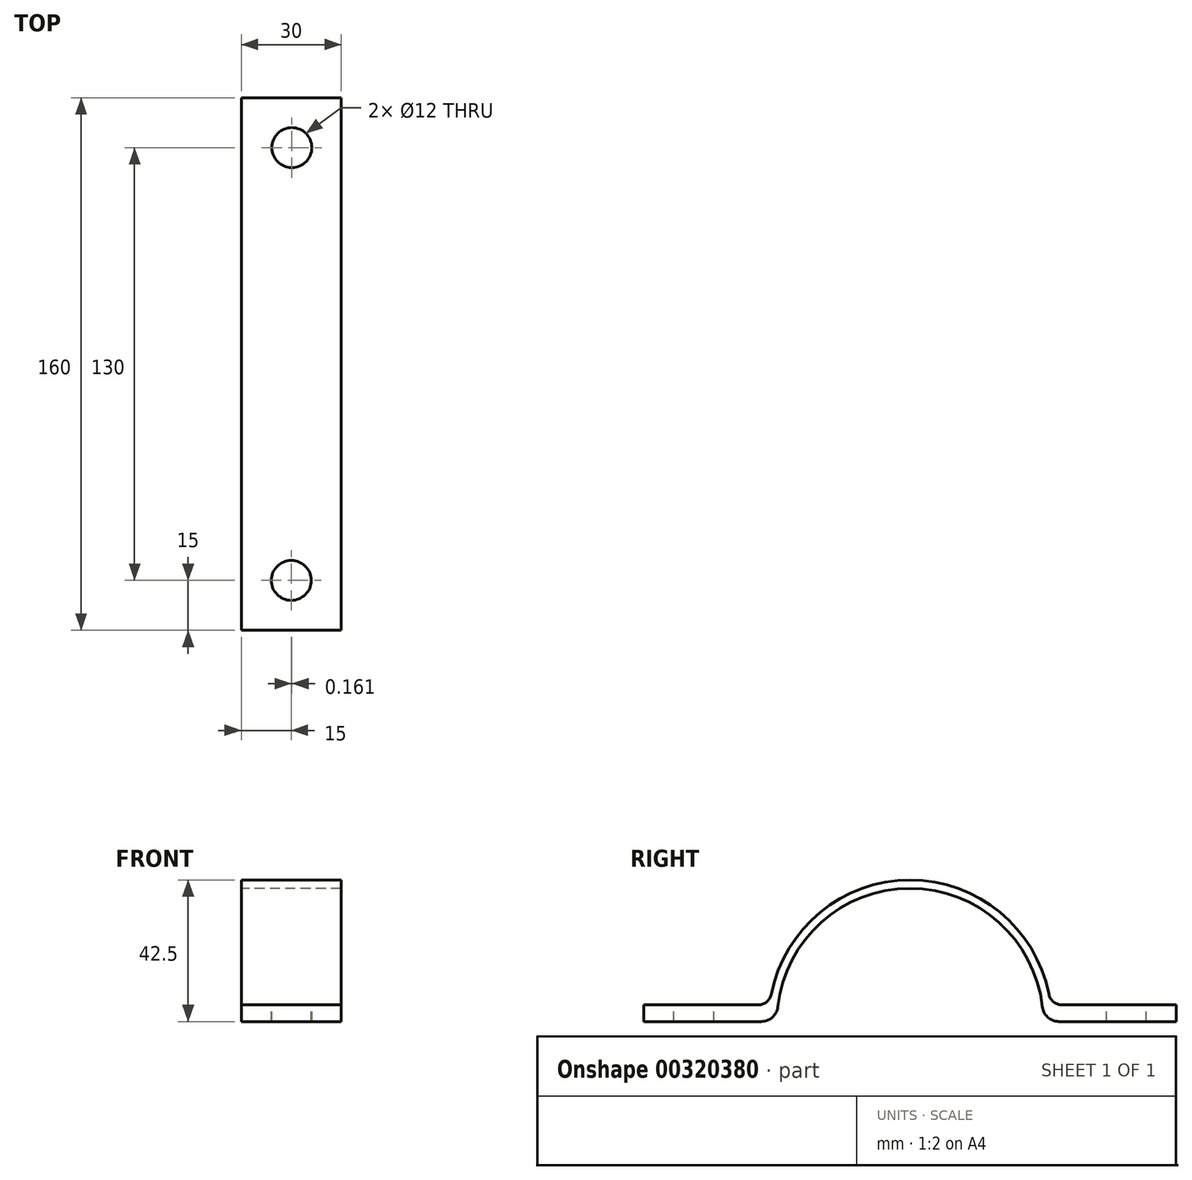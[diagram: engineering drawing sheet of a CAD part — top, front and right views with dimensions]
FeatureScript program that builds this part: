
annotation { "Feature Type Name" : "Feature", "Feature Type Description" : "" }
export const myFeature = defineFeature(function(context is Context, id is Id, definition is map)
    precondition{}
    {
        {
            var Q0;
            Q0=qCreatedBy(makeId("Right.planeOp"),FACE);
            var sketch = newSketch(context, id + "F0", { "sketchPlane" : qUnion([Q0])});
            skArc(sketch, "E0", {"start": v(42.2, 5) * mm, "mid": v(0, 42.5) * mm, "end": v(-42.2, 5) * mm});
            skArc(sketch, "E1", {"start": v(40, 0) * mm, "mid": v(0, 40) * mm, "end": v(-40, 0) * mm});
            skLineSegment(sketch, "E2.bottom", {"start": v(-80, 0) * mm, "end": v(-40, 0) * mm});
            skLineSegment(sketch, "E3.trimOffspring", {"start": v(40, 0) * mm, "end": v(80, 0) * mm});
            skLineSegment(sketch, "E4.top", {"start": v(-80, 5) * mm, "end": v(-42.2, 5) * mm});
            skLineSegment(sketch, "E4.left", {"start": v(-80, 0) * mm, "end": v(-80, 5) * mm});
            skLineSegment(sketch, "E4.right", {"start": v(80, 0) * mm, "end": v(80, 5) * mm});
            skLineSegment(sketch, "E5.trimOffspring", {"start": v(42.2, 5) * mm, "end": v(80, 5) * mm});
            skSolve(sketch);
        }
        {
            var Q0;
            Q0=makeQuery(id+"F0.imprint","IMPRINT",FACE,{"disambiguationData":[TD([[makeQuery(id+"F0.imprint","IMPRINT",EDGE,{"derivedFrom":sQuery(id+"F0.wireOp",EDGE,"E0")}),1.0]])]});
            extrude(context, id + "F1", {"entities" : qUnion([Q0]), "depth" : 30 * mm});
        }
        {
            var Q0;
            Q0=makeQuery(id+"F1.opExtrude","SWEPT_EDGE",EDGE,{"disambiguationData":[OSD([sQuery(id+"F0.wireOp",EDGE,"E0"),sQuery(id+"F0.wireOp",EDGE,"E4.top")])]});
            var Q1;
            Q1=makeQuery(id+"F1.opExtrude","SWEPT_EDGE",EDGE,{"disambiguationData":[OSD([sQuery(id+"F0.wireOp",EDGE,"E0"),sQuery(id+"F0.wireOp",EDGE,"E5.trimOffspring")])]});
            fillet(context, id + "F2", {"entities" : qUnion([Q0, Q1]), "radius" : 4 * mm, "tangentPropagation" : true, "allowEdgeOverflow" : false});
        }
        {
            var Q0;
            Q0=makeQuery(id+"F1.opExtrude","SWEPT_EDGE",EDGE,{"disambiguationData":[OSD([sQuery(id+"F0.wireOp",EDGE,"E1"),sQuery(id+"F0.wireOp",EDGE,"E2.bottom")])]});
            var Q1;
            Q1=makeQuery(id+"F1.opExtrude","SWEPT_EDGE",EDGE,{"disambiguationData":[OSD([sQuery(id+"F0.wireOp",EDGE,"E1"),sQuery(id+"F0.wireOp",EDGE,"E3.trimOffspring")])]});
            fillet(context, id + "F3", {"entities" : qUnion([Q0, Q1]), "radius" : 5 * mm, "tangentPropagation" : true, "allowEdgeOverflow" : false});
        }
        {
            var Q0;
            Q0=makeQuery(id+"F1.opExtrude","SWEPT_FACE",FACE,{"disambiguationData":[OSD([sQuery(id+"F0.wireOp",EDGE,"E4.top")])]});
            var sketch = newSketch(context, id + "F4", { "sketchPlane" : qUnion([Q0])});
            skCircle(sketch, "E6", {"center": v(15, -65) * mm, "radius": 6 * mm});
            skPoint(sketch, "E6.centerSnap0", {"position": v(30, -65) * mm});
            skPoint(sketch, "E6.centerSnap1", {"position": v(15, -80) * mm});
            skCircle(sketch, "E7", {"center": v(15.16, 65) * mm, "radius": 6 * mm});
            skPoint(sketch, "E7.centerSnap0", {"position": v(15.16, -43.43) * mm});
            skSolve(sketch);
        }
        {
            var Q0;
            Q0=makeQuery(id+"F4.imprint","IMPRINT",FACE,{"disambiguationData":[TD([[makeQuery(id+"F4.imprint","IMPRINT",EDGE,{"derivedFrom":sQuery(id+"F4.wireOp",EDGE,"E6")}),1.0]])]});
            var Q1;
            Q1=makeQuery(id+"F4.imprint","IMPRINT",FACE,{"disambiguationData":[TD([[makeQuery(id+"F4.imprint","IMPRINT",EDGE,{"derivedFrom":sQuery(id+"F4.wireOp",EDGE,"E7")}),1.0]])]});
            extrude(context, id + "F5", {"entities" : qUnion([Q0, Q1]), "operationType" : NewBodyOperationType.REMOVE, "oppositeDirection" : true, "depth" : 25 * mm});
        }
    });
